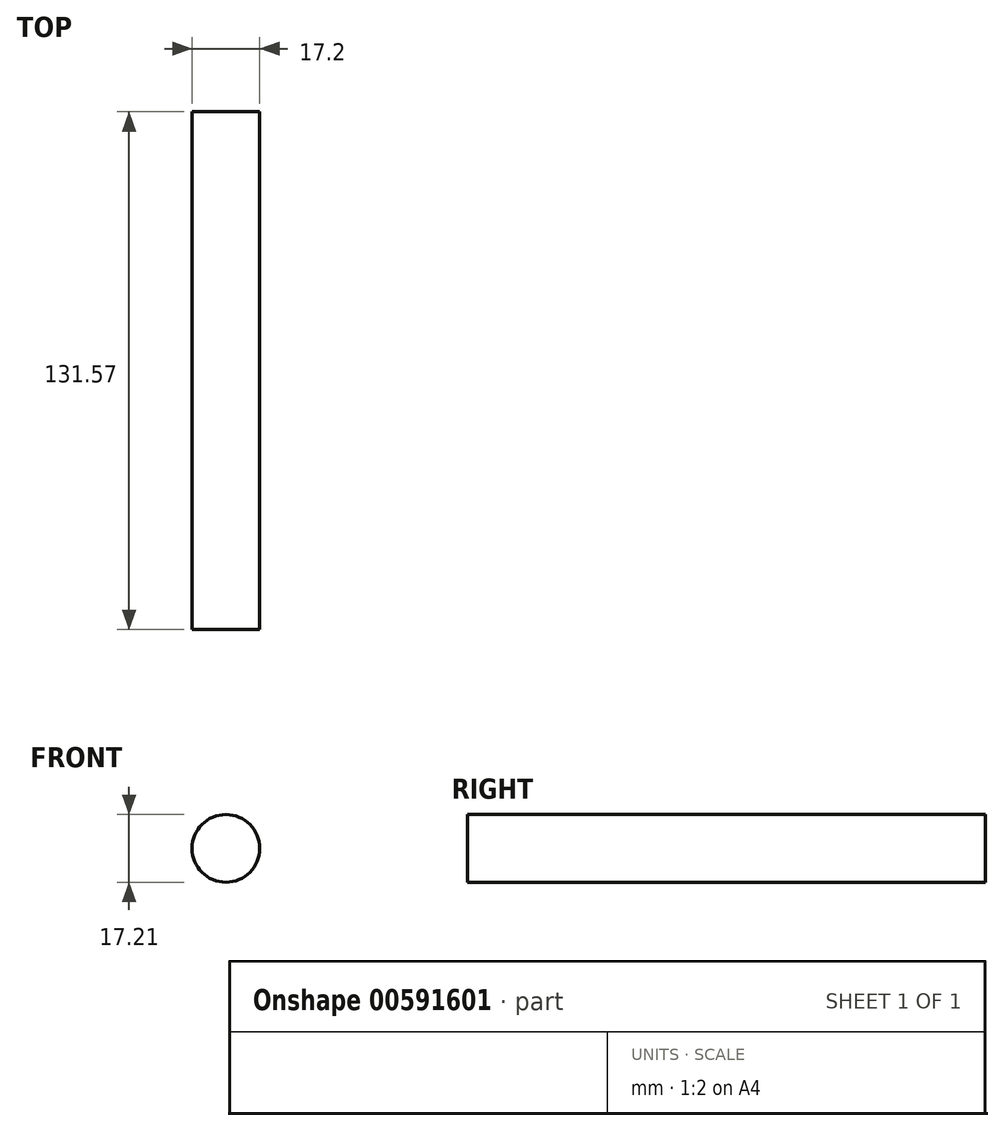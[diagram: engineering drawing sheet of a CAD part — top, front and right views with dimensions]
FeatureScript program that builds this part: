
annotation { "Feature Type Name" : "Feature", "Feature Type Description" : "" }
export const myFeature = defineFeature(function(context is Context, id is Id, definition is map)
    precondition{}
    {
        {
            var Q0;
            Q0=qCreatedBy(makeId("Front.planeOp"),FACE);
            var sketch = newSketch(context, id + "F0", { "sketchPlane" : qUnion([Q0])});
            skCircle(sketch, "E0", {"center": v(-32.14, 27.05) * mm, "radius": 8.6 * mm});
            skSolve(sketch);
        }
        {
            var Q0;
            Q0=makeQuery(id+"F0.imprint","IMPRINT",FACE,{"disambiguationData":[TD([[makeQuery(id+"F0.imprint","IMPRINT",EDGE,{"derivedFrom":sQuery(id+"F0.wireOp",EDGE,"E0")}),1.0]])]});
            extrude(context, id + "F1", {"entities" : qUnion([Q0]), "depth" : 131.57 * mm, "offsetDistance" : 25.4 * mm});
        }
    });
